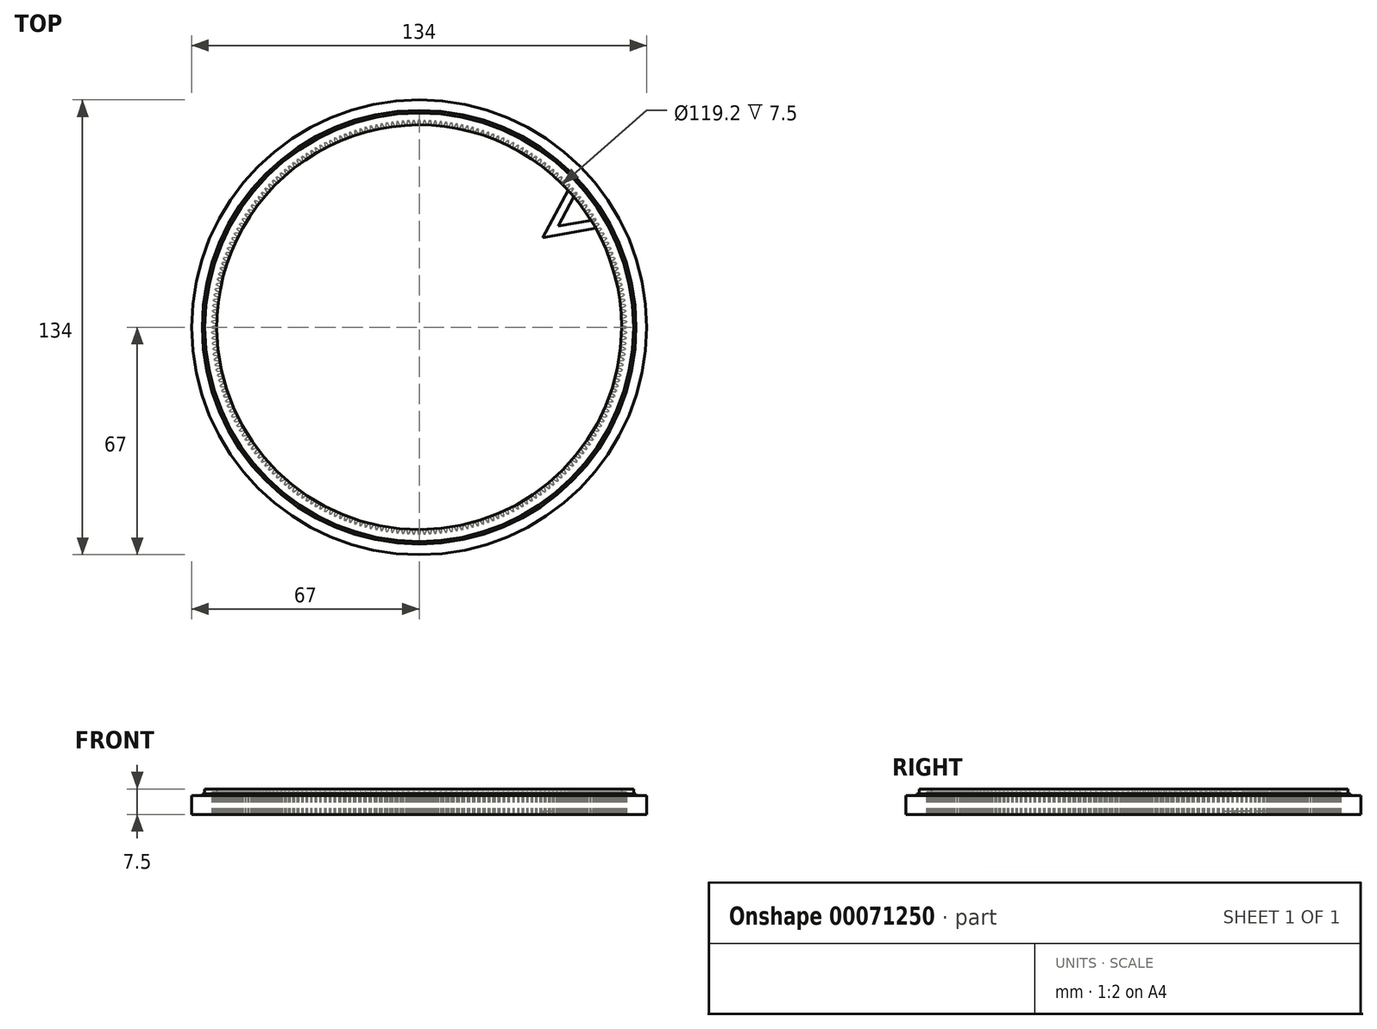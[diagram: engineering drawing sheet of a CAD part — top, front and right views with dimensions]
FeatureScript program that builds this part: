
annotation { "Feature Type Name" : "Feature", "Feature Type Description" : "" }
export const myFeature = defineFeature(function(context is Context, id is Id, definition is map)
    precondition{}
    {
        {
            var Q0;
            Q0=qCreatedBy(makeId("Top.planeOp"),FACE);
            var sketch = newSketch(context, id + "F0", { "sketchPlane" : qUnion([Q0])});
            skCircle(sketch, "E0", {"center": v(0, 0) * mm, "radius": 59.6 * mm});
            skCircle(sketch, "E1", {"center": v(0, 0) * mm, "radius": 67 * mm});
            skSolve(sketch);
        }
        {
            var Q0;
            Q0=makeQuery(id+"F0.imprint","IMPRINT",FACE,{"disambiguationData":[TD([[makeQuery(id+"F0.imprint","IMPRINT",EDGE,{"derivedFrom":sQuery(id+"F0.wireOp",EDGE,"E0")}),-1.0]])]});
            extrude(context, id + "F1", {"entities" : qUnion([Q0]), "endBound" : BoundingType.SYMMETRIC, "depth" : 7.5 * mm});
        }
        {
            var Q0;
            Q0=makeQuery(id+"F1.opExtrude","CAP_FACE",FACE,{"disambiguationData":[OSD([sQuery(id+"F0.wireOp",EDGE,"E0"),sQuery(id+"F0.wireOp",EDGE,"E1")])],"isStart":false});
            var sketch = newSketch(context, id + "F2", { "sketchPlane" : qUnion([Q0])});
            skCircle(sketch, "E2", {"center": v(0, 0) * mm, "radius": 63.12 * mm});
            skCircle(sketch, "E3", {"center": v(0, 0) * mm, "radius": 63.88 * mm});
            skSolve(sketch);
        }
        {
            var Q0;
            Q0=makeQuery(id+"F2.imprint","IMPRINT",FACE,{"disambiguationData":[TD([[makeQuery(id+"F2.imprint","IMPRINT",EDGE,{"derivedFrom":sQuery(id+"F2.wireOp",EDGE,"E2")}),-1.0]])]});
            extrude(context, id + "F3", {"entities" : qUnion([Q0]), "operationType" : NewBodyOperationType.REMOVE, "oppositeDirection" : true, "depth" : 1.5 * mm});
        }
        {
            var Q0;
            Q0=makeQuery(id+"F2.imprint","IMPRINT",FACE,{"disambiguationData":[TD([[makeQuery(id+"F2.imprint","IMPRINT",EDGE,{"derivedFrom":sQuery(id+"F2.wireOp",EDGE,"E3")}),-1.0]])]});
            extrude(context, id + "F4", {"entities" : qUnion([Q0]), "operationType" : NewBodyOperationType.REMOVE, "oppositeDirection" : true, "depth" : 2 * mm});
        }
        {
            var Q0;
            Q0=makeQuery(id+"F1.opExtrude","CAP_FACE",FACE,{"disambiguationData":[OSD([sQuery(id+"F0.wireOp",EDGE,"E0"),sQuery(id+"F0.wireOp",EDGE,"E1")])],"isStart":true});
            var sketch = newSketch(context, id + "F5", { "sketchPlane" : qUnion([Q0])});
            skCircle(sketch, "E4", {"center": v(0, 0) * mm, "radius": 61 * mm, "construction": true});
            skLineSegment(sketch, "E5", {"start": v(0, 0) * mm, "end": v(61, 0) * mm, "construction": true});
            skLineSegment(sketch, "E6", {"start": v(61, 0) * mm, "end": v(59.4, 0) * mm, "construction": true});
            skLineSegment(sketch, "E7", {"start": v(59.4, 0.68) * mm, "end": v(59.4, -0.67) * mm});
            skLineSegment(sketch, "E8", {"start": v(61, -0.15) * mm, "end": v(61, 0.15) * mm});
            skLineSegment(sketch, "E9", {"start": v(59.4, 0.68) * mm, "end": v(61, 0.15) * mm});
            skLineSegment(sketch, "E10", {"start": v(61, -0.15) * mm, "end": v(59.4, -0.67) * mm});
            skSolve(sketch);
        }
        {
            var Q0;
            Q0 = qSketchRegion(id + "F5", true);
            extrude(context, id + "F6", {"entities" : qUnion([Q0]), "operationType" : NewBodyOperationType.REMOVE, "oppositeDirection" : true, "depth" : 6.5 * mm});
        }
        {
            var Q0;
            Q0=makeQuery(id+"F6.boolean.opBoolean","COPY",FACE,{"derivedFrom":makeQuery(id+"F6.opExtrude","SWEPT_FACE",FACE,{"disambiguationData":[OSD([sQuery(id+"F5.wireOp",EDGE,"E10")])]})});
            var Q1;
            Q1=makeQuery(id+"F6.boolean.opBoolean","COPY",FACE,{"derivedFrom":makeQuery(id+"F6.opExtrude","CAP_FACE",FACE,{"disambiguationData":[OSD([sQuery(id+"F5.wireOp",EDGE,"E7"),sQuery(id+"F5.wireOp",EDGE,"E8"),sQuery(id+"F5.wireOp",EDGE,"E9"),sQuery(id+"F5.wireOp",EDGE,"E10")])],"isStart":false})});
            var Q2;
            Q2=makeQuery(id+"F6.boolean.opBoolean","COPY",FACE,{"derivedFrom":makeQuery(id+"F6.opExtrude","SWEPT_FACE",FACE,{"disambiguationData":[OSD([sQuery(id+"F5.wireOp",EDGE,"E8")])]})});
            var Q3;
            Q3=makeQuery(id+"F6.boolean.opBoolean","COPY",FACE,{"derivedFrom":makeQuery(id+"F6.opExtrude","SWEPT_FACE",FACE,{"disambiguationData":[OSD([sQuery(id+"F5.wireOp",EDGE,"E9")])]})});
            var Q4;
            Q4=makeQuery(id+"F1.opExtrude","CAP_EDGE",EDGE,{"disambiguationData":[OSD([sQuery(id+"F0.wireOp",EDGE,"E1")])],"isStart":true});
            circularPattern(context, id + "F7", {"faces" : qUnion([Q0, Q1, Q2, Q3]), "axis" : qUnion([Q4]), "angle" : 360 * degree, "instanceCount" : 240, "equalSpace" : true, "patternType" : PatternType.FACE});
        }
        {
            var Q0;
            Q0=makeQuery(id+"F1.opExtrude","CAP_FACE",FACE,{"disambiguationData":[OSD([sQuery(id+"F0.wireOp",EDGE,"E0"),sQuery(id+"F0.wireOp",EDGE,"E1")])],"isStart":true});
            var sketch = newSketch(context, id + "F8", { "sketchPlane" : qUnion([Q0])});
            skCircle(sketch, "E11", {"center": v(0, 0) * mm, "radius": 63.12 * mm});
            skCircle(sketch, "E12.0", {"center": v(0, 0) * mm, "radius": 63.12 * mm, "construction": true});
            skLineSegment(sketch, "E13", {"start": v(0, 0) * mm, "end": v(36.41, -26.44) * mm, "construction": true});
            skLineSegment(sketch, "E14", {"start": v(36.41, -26.44) * mm, "end": v(51.08, -37.1) * mm, "construction": true});
            skLineSegment(sketch, "E15", {"start": v(51.08, -37.1) * mm, "end": v(45.86, -44.27) * mm});
            skLineSegment(sketch, "E16", {"start": v(45.86, -44.27) * mm, "end": v(0, 0) * mm, "construction": true});
            skLineSegment(sketch, "E17", {"start": v(36.41, -26.44) * mm, "end": v(45.86, -44.27) * mm});
            skLineSegment(sketch, "E18.MirrorCS", {"start": v(36.41, -26.44) * mm, "end": v(56.3, -29.91) * mm});
            skLineSegment(sketch, "E19.MirrorCS", {"start": v(51.08, -37.1) * mm, "end": v(56.3, -29.91) * mm});
            skLineSegment(sketch, "E20", {"start": v(46.2, -39.56) * mm, "end": v(41.01, -29.78) * mm});
            skLineSegment(sketch, "E21", {"start": v(41.01, -29.78) * mm, "end": v(51.91, -31.69) * mm});
            skLineSegment(sketch, "E22", {"start": v(51.91, -31.69) * mm, "end": v(46.2, -39.56) * mm});
            skSolve(sketch);
        }
        {
            var Q0;
            {var subQ20=sQuery(id+"F8.wireOp",EDGE,"E20");Q0=makeQuery(id+"F8.imprint","IMPRINT",FACE,{"disambiguationData":[TD([[makeQuery(id+"F8.imprint","IMPRINT",EDGE,{"derivedFrom":subQ20}),1.0]])]});}
            var Q1;
            {var subQ3=makeQuery(id+"F6.boolean.opBoolean","COPY",EDGE,{"derivedFrom":makeQuery(id+"F6.opExtrude","CAP_EDGE",EDGE,{"disambiguationData":[OSD([sQuery(id+"F5.wireOp",EDGE,"E8")])],"isStart":true})});Q1=makeQuery(id+"F8.imprint","IMPRINT",FACE,{"disambiguationData":[TD([[makeQuery(id+"F8.imprint","IMPRINT",EDGE,{"derivedFrom":makeQuery(id+"F7.opPattern","COPY",EDGE,{"derivedFrom":subQ3,"instanceName":"20"})}),-1.0]])]});}
            extrude(context, id + "F9", {"entities" : qUnion([Q0, Q1]), "operationType" : NewBodyOperationType.ADD, "oppositeDirection" : true, "depth" : 1 * mm});
        }
    });
